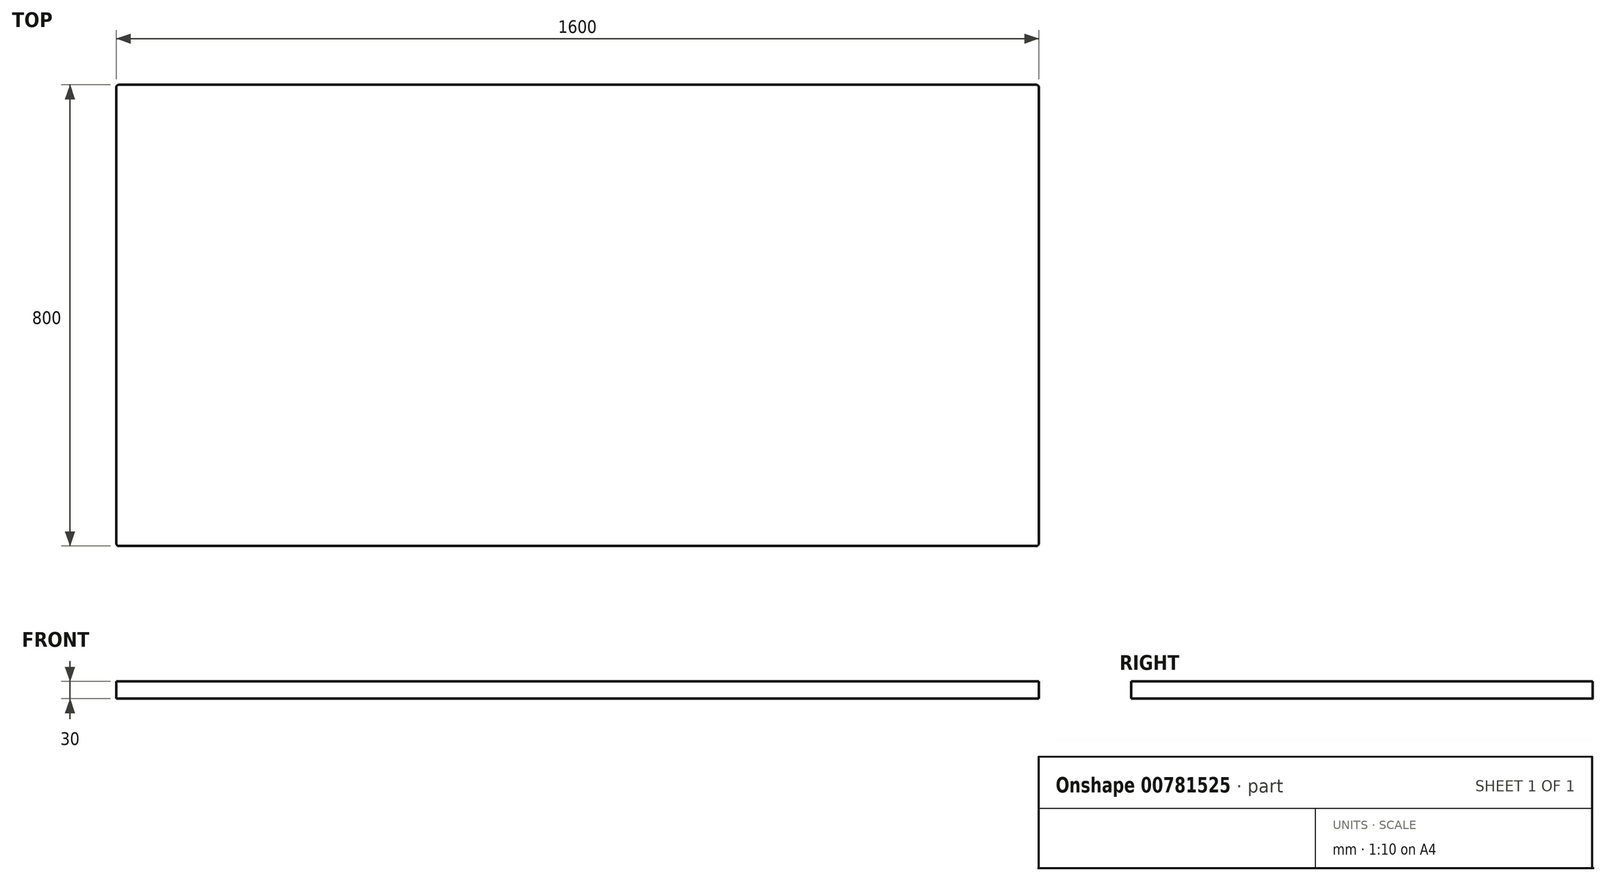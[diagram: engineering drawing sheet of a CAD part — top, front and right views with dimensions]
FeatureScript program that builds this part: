
annotation { "Feature Type Name" : "Feature", "Feature Type Description" : "" }
export const myFeature = defineFeature(function(context is Context, id is Id, definition is map)
    precondition{}
    {
        {
            var Q0;
            Q0=qCreatedBy(makeId("Top.planeOp"),FACE);
            var sketch = newSketch(context, id + "F0", { "sketchPlane" : qUnion([Q0])});
            skLineSegment(sketch, "E0.bottom", {"start": v(0, 0) * mm, "end": v(1600, 0) * mm});
            skLineSegment(sketch, "E0.top", {"start": v(0, 800) * mm, "end": v(1600, 800) * mm});
            skLineSegment(sketch, "E0.left", {"start": v(0, 0) * mm, "end": v(0, 800) * mm});
            skLineSegment(sketch, "E0.right", {"start": v(1600, 0) * mm, "end": v(1600, 800) * mm});
            skSolve(sketch);
        }
        {
            var Q0;
            Q0=makeQuery(id+"F0.imprint","IMPRINT",FACE,{"disambiguationData":[TD([[makeQuery(id+"F0.imprint","IMPRINT",EDGE,{"derivedFrom":sQuery(id+"F0.wireOp",EDGE,"E0.bottom")}),1.0]])]});
            extrude(context, id + "F1", {"entities" : qUnion([Q0]), "depth" : 30 * mm, "offsetDistance" : 25.4 * mm});
        }
        {
            var Q0;
            Q0=makeQuery(id+"F1.opExtrude","SWEPT_EDGE",EDGE,{"disambiguationData":[OSD([sQuery(id+"F0.wireOp",EDGE,"E0.bottom"),sQuery(id+"F0.wireOp",EDGE,"E0.left")])]});
            var Q1;
            Q1=makeQuery(id+"F1.opExtrude","SWEPT_EDGE",EDGE,{"disambiguationData":[OSD([sQuery(id+"F0.wireOp",EDGE,"E0.bottom"),sQuery(id+"F0.wireOp",EDGE,"E0.right")])]});
            var Q2;
            Q2=makeQuery(id+"F1.opExtrude","SWEPT_EDGE",EDGE,{"disambiguationData":[OSD([sQuery(id+"F0.wireOp",EDGE,"E0.top"),sQuery(id+"F0.wireOp",EDGE,"E0.left")])]});
            var Q3;
            Q3=makeQuery(id+"F1.opExtrude","SWEPT_EDGE",EDGE,{"disambiguationData":[OSD([sQuery(id+"F0.wireOp",EDGE,"E0.top"),sQuery(id+"F0.wireOp",EDGE,"E0.right")])]});
            fillet(context, id + "F2", {"entities" : qUnion([Q0, Q1, Q2, Q3]), "radius" : 5 * mm, "tangentPropagation" : true, "allowEdgeOverflow" : false});
        }
    });
